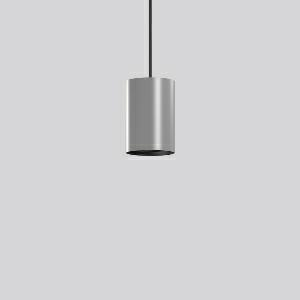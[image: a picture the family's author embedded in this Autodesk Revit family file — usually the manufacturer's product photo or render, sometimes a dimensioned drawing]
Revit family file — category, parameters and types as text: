
# Revit family: deecos_p_maxi_911538_004_2_de81
name_source: partatom
category: Lighting Fixtures
units: mm (PartAtom-declared; Revit-internal decimal feet)

## family parameters
Cut with Voids When Loaded = No
Host = Face
Light Source = No
Part Type = Normal
Room Calculation Point = No
Round Connector Dimension = Use Diameter
Shared = No

## types (1)
- DEECOS P maxi (1 x LED Modul 927, 4100 lm, 2700)
    Apparent Load = 35 VA
    Approval mark = CE
    CIE Flux Codes = 100 100 100 100 100
    Color Rendering = 92
    Color Temperature = 2700
    Default Elevation = 1800 mm
    Description = Series: DEECOS P maxi
Cylindrical pendant luminaire. Housing: die-cast aluminium, powder-coated. Canopy made of powder-coated sheet steel with magnetic attachment. Optical assembly with reflector made of MIRO-Silver with 98% total light reflection for outstanding efficiency - can be changed without tools. Best colour rendering index Ra>90. Transparent suspension cable 2 m, can be shortened. High quality converter without flickering and stroboscopic effect. The following accessories can be mounted without use of tools: interchangeable lenses, honeycomb louvre, clear and frosted diffusers, white interchangeable plastic ring. Decorative recessed suspension set available as accessory. 
Colour: silver
Diameter: 123 mm
Height: 181 mm
Suspension length: 2000 mm
Lamp: LED
Socket: without socket
Colour temperature: 2700K
Colour rendering index (CRI): 92
System power: 35 W
Rated luminous flux: 4100 lm
Luminous efficiency: 117 lm/W
Control gear: Regulated power supply
Protection class: I
Type of protection: IP 20
    Height = 181 mm
    Lamp = 1 x LED Modul 927
    Lamp Light Flux = 4100 lm
    Lamp count = 1
    Length = 123 mm
    Lifetime = 50000 h
    Luminous efficacy = 117 lm/W
    Manufacturer = RZB
    ModVariant = No
    Model = 911538.004.2
    Mounting Place = Ceiling
    Mounting Type = Pendant
    Number of Poles = 1
    OnlyDefault = Yes
    Power Factor = 1
    Product Name = DEECOS P maxi
    Product group = Pendant luminaires
    ProductGroupID = 902
    Protection Class = Protection class I
    Protection Degree = IP 20
    RLX_Detail_Level = 1
    RLX_Emergency_Light_Flux = 0 lm
    RLX_Emergency_Type = 0
    RLX_Emergency_Type_DB = No
    RlxData = <blob elided: 35573 chars, md5=6757729d>
    Socket = socket
    Standby Power = 0 W
    System Light Flux = 4100 lm
    System Power = 35 W
    Type Comments = Product without accessories
    Type Image = 911480.004.jpg
    URL = http://relux.com
    VarID = ---
    Voltage = 230 V
    Voltage Range = 220-240 V
    Weight = 0.00 kg
    Width = 0 mm  [stored 0 ft]

note: [stored X ft] marks values corroborated as IEEE doubles in the binary element streams (Revit-internal decimal feet)

## geometry (parser evidence)
native form markers: Blend x4, Sweep x7
no freeform markers — native parametric forms only
